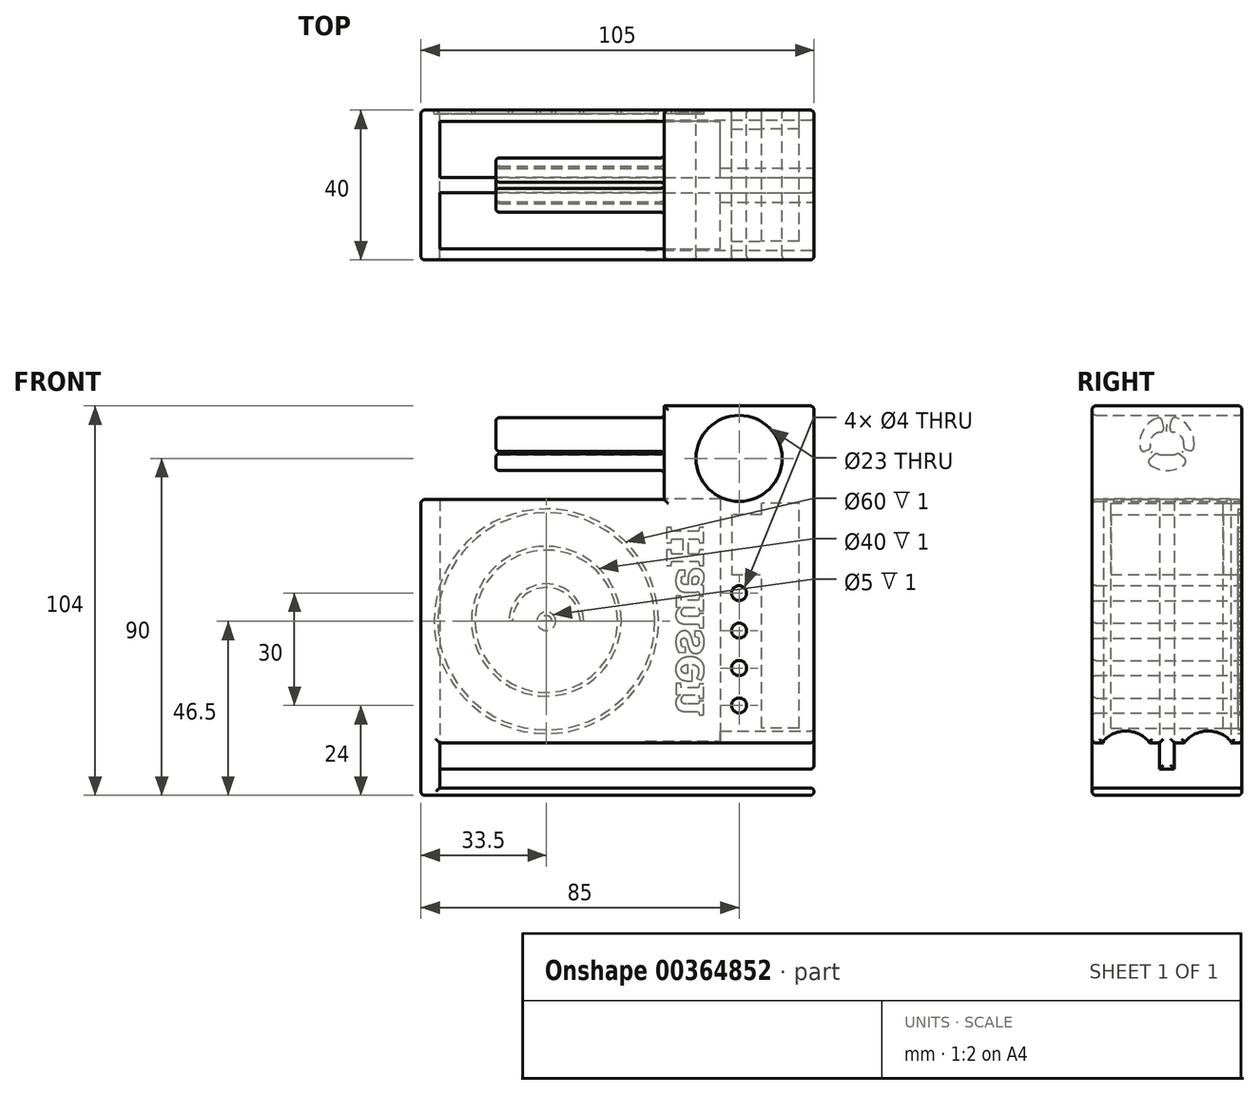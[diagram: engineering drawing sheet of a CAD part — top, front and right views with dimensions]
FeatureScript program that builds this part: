
annotation { "Feature Type Name" : "Feature", "Feature Type Description" : "" }
export const myFeature = defineFeature(function(context is Context, id is Id, definition is map)
    precondition{}
    {
        {
            var Q0;
            Q0=qCreatedBy(makeId("Front.planeOp"),FACE);
            var sketch = newSketch(context, id + "F0", { "sketchPlane" : qUnion([Q0])});
            skLineSegment(sketch, "E0.bottom", {"start": v(20, -45) * mm, "end": v(-20, -45) * mm});
            skLineSegment(sketch, "E0.top", {"start": v(20, 45) * mm, "end": v(-20, 45) * mm});
            skLineSegment(sketch, "E0.left", {"start": v(20, -45) * mm, "end": v(20, 45) * mm});
            skLineSegment(sketch, "E0.right", {"start": v(-20, -45) * mm, "end": v(-20, 45) * mm});
            skPoint(sketch, "E0.middle", {"position": v(0, 0) * mm});
            skLineSegment(sketch, "E1", {"start": v(0, 45) * mm, "end": v(0, 31) * mm});
            skCircle(sketch, "E2", {"center": v(0, 31) * mm, "radius": 11.5 * mm});
            skLineSegment(sketch, "E3", {"start": v(0, -45) * mm, "end": v(0, -35) * mm});
            skLineSegment(sketch, "E4", {"start": v(0, -35) * mm, "end": v(0, -25) * mm});
            skLineSegment(sketch, "E5", {"start": v(0, -25) * mm, "end": v(0, -15) * mm});
            skLineSegment(sketch, "E6", {"start": v(0, -15) * mm, "end": v(0, -5) * mm});
            skLineSegment(sketch, "E7", {"start": v(0, -5) * mm, "end": v(0, 5) * mm});
            skCircle(sketch, "E8", {"center": v(0, -35) * mm, "radius": 2 * mm});
            skCircle(sketch, "E9", {"center": v(0, -25) * mm, "radius": 2 * mm});
            skCircle(sketch, "E10", {"center": v(0, -15) * mm, "radius": 2 * mm});
            skCircle(sketch, "E11", {"center": v(0, -5) * mm, "radius": 2 * mm});
            skSolve(sketch);
        }
        {
            var Q0;
            {var subQ9=sQuery(id+"F0.wireOp",EDGE,"E0.left");Q0=makeQuery(id+"F0.imprint","IMPRINT",FACE,{"disambiguationData":[TD([[makeQuery(id+"F0.imprint","IMPRINT",EDGE,{"derivedFrom":subQ9}),1.0]])]});}
            extrude(context, id + "F1", {"entities" : qUnion([Q0]), "depth" : 40 * mm});
        }
        {
            var Q0;
            Q0=makeQuery(id+"F1.opExtrude","SWEPT_FACE",FACE,{"disambiguationData":[OSD([sQuery(id+"F0.wireOp",EDGE,"E0.right")])]});
            var sketch = newSketch(context, id + "F2", { "sketchPlane" : qUnion([Q0])});
            skLineSegment(sketch, "E12", {"start": v(20, 35) * mm, "end": v(7.42, 30.91) * mm});
            skLineSegment(sketch, "E13", {"start": v(20, 35) * mm, "end": v(21.83, 43.62) * mm});
            skLineSegment(sketch, "E14", {"start": v(20, 35) * mm, "end": v(30.16, 25.85) * mm});
            skCircle(sketch, "E15", {"center": v(20, 35) * mm, "radius": 7.25 * mm});
            skLineSegment(sketch, "E16", {"start": v(20, 35) * mm, "end": v(20, 38) * mm});
            skLineSegment(sketch, "E17", {"start": v(20, 38) * mm, "end": v(18.5, 38) * mm});
            skLineSegment(sketch, "E18", {"start": v(18.5, 38) * mm, "end": v(21.5, 38) * mm});
            skPoint(sketch, "E18.endSnap0", {"position": v(19.25, 38) * mm});
            skLineSegment(sketch, "E19", {"start": v(21.5, 38) * mm, "end": v(21.5, 32) * mm});
            skLineSegment(sketch, "E20", {"start": v(21.5, 32) * mm, "end": v(18.5, 32) * mm});
            skLineSegment(sketch, "E21", {"start": v(18.5, 32) * mm, "end": v(18.5, 38) * mm});
            skArc(sketch, "E22", {"start": v(18.5, 38) * mm, "mid": v(15.5, 35) * mm, "end": v(18.5, 32) * mm});
            skArc(sketch, "E23", {"start": v(21.5, 32) * mm, "mid": v(24.5, 35) * mm, "end": v(21.5, 38) * mm});
            skLineSegment(sketch, "E24", {"start": v(8.8, 25.44) * mm, "end": v(20, 35) * mm});
            skLineSegment(sketch, "E25", {"start": v(20, 35) * mm, "end": v(31.2, 31.03) * mm});
            skLineSegment(sketch, "E26", {"start": v(20, 35) * mm, "end": v(23.11, 43.8) * mm, "construction": true});
            skLineSegment(sketch, "E27", {"start": v(20, 35) * mm, "end": v(18.34, 43.94) * mm});
            skLineSegment(sketch, "E28", {"start": v(0, 45) * mm, "end": v(40, 45) * mm});
            skLineSegment(sketch, "E29", {"start": v(40, 45) * mm, "end": v(20, 45) * mm});
            skLineSegment(sketch, "E30", {"start": v(20, 45) * mm, "end": v(20, 35) * mm});
            skSolve(sketch);
        }
        {
            var Q0;
            {var subQ5=sQuery(id+"F2.wireOp",EDGE,"E12");var subQ7=sQuery(id+"F2.wireOp",EDGE,"E15");var subQ8=makeQuery(id+"F2.imprint","INTERSECT",VERTEX,{"derivedFrom":[subQ5,subQ7]});Q0=makeQuery(id+"F2.imprint","IMPRINT",FACE,{"disambiguationData":[TD([[makeQuery(id+"F2.imprint","IMPRINT",EDGE,{"disambiguationData":[TD([[subQ8,1.0]])],"derivedFrom":subQ5}),-1.0]])]});}
            var Q1;
            {var subQ1=sQuery(id+"F2.wireOp",EDGE,"E20");Q1=makeQuery(id+"F2.imprint","IMPRINT",FACE,{"disambiguationData":[TD([[makeQuery(id+"F2.imprint","IMPRINT",EDGE,{"derivedFrom":subQ1}),1.0]])]});}
            var Q2;
            {var subQ1=sQuery(id+"F2.wireOp",EDGE,"E18");var subQ5=sQuery(id+"F2.wireOp",EDGE,"E13");var subQ6=makeQuery(id+"F2.imprint","INTERSECT",VERTEX,{"derivedFrom":[subQ5,subQ1]});Q2=makeQuery(id+"F2.imprint","IMPRINT",FACE,{"disambiguationData":[TD([[makeQuery(id+"F2.imprint","IMPRINT",EDGE,{"disambiguationData":[TD([[subQ6,-1.0]])],"derivedFrom":subQ5}),-1.0]])]});}
            extrude(context, id + "F3", {"entities" : qUnion([Q0, Q1, Q2]), "operationType" : NewBodyOperationType.ADD, "depth" : 45 * mm});
        }
        {
            var Q0;
            Q0=makeQuery(id+"F3.opExtrude","SWEPT_EDGE",EDGE,{"disambiguationData":[OSD([sQuery(id+"F2.wireOp",EDGE,"E15"),sQuery(id+"F2.wireOp",EDGE,"E27")])]});
            var Q1;
            Q1=makeQuery(id+"F3.opExtrude","SWEPT_EDGE",EDGE,{"disambiguationData":[OSD([sQuery(id+"F2.wireOp",EDGE,"E13"),sQuery(id+"F2.wireOp",EDGE,"E15")])]});
            var Q2;
            Q2=makeQuery(id+"F3.opExtrude","SWEPT_EDGE",EDGE,{"disambiguationData":[OSD([sQuery(id+"F2.wireOp",EDGE,"E13"),sQuery(id+"F2.wireOp",EDGE,"E18")])]});
            var Q3;
            Q3=makeQuery(id+"F3.opExtrude","SWEPT_EDGE",EDGE,{"disambiguationData":[OSD([sQuery(id+"F2.wireOp",EDGE,"E12"),sQuery(id+"F2.wireOp",EDGE,"E15")])]});
            var Q4;
            Q4=makeQuery(id+"F3.opExtrude","SWEPT_EDGE",EDGE,{"disambiguationData":[OSD([sQuery(id+"F2.wireOp",EDGE,"E18"),sQuery(id+"F2.wireOp",EDGE,"E27")])]});
            var Q5;
            Q5=makeQuery(id+"F3.opExtrude","SWEPT_EDGE",EDGE,{"disambiguationData":[OSD([sQuery(id+"F2.wireOp",EDGE,"E12"),sQuery(id+"F2.wireOp",EDGE,"E22")])]});
            var Q6;
            Q6=makeQuery(id+"F3.opExtrude","SWEPT_EDGE",EDGE,{"disambiguationData":[OSD([sQuery(id+"F2.wireOp",EDGE,"E22"),sQuery(id+"F2.wireOp",EDGE,"E24")])]});
            var Q7;
            Q7=makeQuery(id+"F3.opExtrude","SWEPT_EDGE",EDGE,{"disambiguationData":[OSD([sQuery(id+"F2.wireOp",EDGE,"E15"),sQuery(id+"F2.wireOp",EDGE,"E24")])]});
            var Q8;
            Q8=makeQuery(id+"F3.opExtrude","SWEPT_EDGE",EDGE,{"disambiguationData":[OSD([sQuery(id+"F2.wireOp",EDGE,"E14"),sQuery(id+"F2.wireOp",EDGE,"E23")])]});
            var Q9;
            Q9=makeQuery(id+"F3.opExtrude","SWEPT_EDGE",EDGE,{"disambiguationData":[OSD([sQuery(id+"F2.wireOp",EDGE,"E14"),sQuery(id+"F2.wireOp",EDGE,"E15")])]});
            var Q10;
            Q10=makeQuery(id+"F3.opExtrude","SWEPT_EDGE",EDGE,{"disambiguationData":[OSD([sQuery(id+"F2.wireOp",EDGE,"E23"),sQuery(id+"F2.wireOp",EDGE,"E25")])]});
            var Q11;
            Q11=makeQuery(id+"F3.opExtrude","SWEPT_EDGE",EDGE,{"disambiguationData":[OSD([sQuery(id+"F2.wireOp",EDGE,"E15"),sQuery(id+"F2.wireOp",EDGE,"E25")])]});
            fillet(context, id + "F4", {"entities" : qUnion([Q0, Q1, Q2, Q3, Q4, Q5, Q6, Q7, Q8, Q9, Q10, Q11]), "radius" : 1 * mm, "tangentPropagation" : true, "allowEdgeOverflow" : false});
        }
        {
            var Q0;
            Q0=makeQuery(id+"F3.opExtrude","CAP_FACE",FACE,{"disambiguationData":[OSD([sQuery(id+"F2.wireOp",EDGE,"E12"),sQuery(id+"F2.wireOp",EDGE,"E15"),sQuery(id+"F2.wireOp",EDGE,"E18"),sQuery(id+"F2.wireOp",EDGE,"E22"),sQuery(id+"F2.wireOp",EDGE,"E27")])],"isStart":false});
            var Q1;
            {var subQ0=sQuery(id+"F2.wireOp",EDGE,"E15");Q1=makeQuery(id+"F3.opExtrude","SWEPT_FACE",FACE,{"disambiguationData":[OSD([subQ0]),TDD([makeQuery(id+"F2.imprint","IMPRINT",EDGE,{"disambiguationData":[TD([[makeQuery(id+"F2.imprint","INTERSECT",VERTEX,{"derivedFrom":[sQuery(id+"F2.wireOp",EDGE,"E12"),subQ0]}),1.0]])],"derivedFrom":subQ0})])]});}
            var Q2;
            {var subQ0=sQuery(id+"F2.wireOp",EDGE,"E15");Q2=makeQuery(id+"F3.opExtrude","SWEPT_FACE",FACE,{"disambiguationData":[OSD([subQ0]),TDD([makeQuery(id+"F2.imprint","IMPRINT",EDGE,{"disambiguationData":[TD([[makeQuery(id+"F2.imprint","INTERSECT",VERTEX,{"derivedFrom":[subQ0,sQuery(id+"F2.wireOp",EDGE,"E25")]}),-1.0]])],"derivedFrom":subQ0})])]});}
            var Q3;
            {var subQ0=sQuery(id+"F2.wireOp",EDGE,"E15");Q3=makeQuery(id+"F3.opExtrude","SWEPT_FACE",FACE,{"disambiguationData":[OSD([subQ0]),TDD([makeQuery(id+"F2.imprint","IMPRINT",EDGE,{"disambiguationData":[TD([[makeQuery(id+"F2.imprint","INTERSECT",VERTEX,{"derivedFrom":[sQuery(id+"F2.wireOp",EDGE,"E14"),subQ0]}),1.0]])],"derivedFrom":subQ0})])]});}
            fillet(context, id + "F5", {"entities" : qUnion([Q0, Q1, Q2, Q3]), "radius" : 1 * mm, "tangentPropagation" : true, "allowEdgeOverflow" : false});
        }
        {
            var Q0;
            Q0=makeQuery(id+"F5.opFillet","SPLIT",FACE,{"disambiguationData":[OD(0.0)],"derivedFrom":makeQuery(id+"F1.opExtrude","SWEPT_FACE",FACE,{"disambiguationData":[OSD([sQuery(id+"F0.wireOp",EDGE,"E0.right")])]})});
            var sketch = newSketch(context, id + "F6", { "sketchPlane" : qUnion([Q0])});
            skLineSegment(sketch, "E31.bottom", {"start": v(0, -45) * mm, "end": v(40, -45) * mm});
            skLineSegment(sketch, "E31.top", {"start": v(0, 20) * mm, "end": v(40, 20) * mm});
            skLineSegment(sketch, "E31.left", {"start": v(0, -45) * mm, "end": v(0, 20) * mm});
            skLineSegment(sketch, "E31.right", {"start": v(40, -45) * mm, "end": v(40, 20) * mm});
            skSolve(sketch);
        }
        {
            var Q0;
            Q0 = qSketchRegion(id + "F6", true);
            extrude(context, id + "F7", {"entities" : qUnion([Q0]), "operationType" : NewBodyOperationType.ADD, "depth" : 65 * mm});
        }
        {
            var Q0;
            Q0=makeQuery(id+"F7.boolean.opBoolean","MERGE",FACE,{"derivedFrom":[makeQuery(id+"F1.opExtrude","SWEPT_FACE",FACE,{"disambiguationData":[OSD([sQuery(id+"F0.wireOp",EDGE,"E0.bottom")])]}),makeQuery(id+"F7.opExtrude","SWEPT_FACE",FACE,{"disambiguationData":[OSD([sQuery(id+"F6.wireOp",EDGE,"E31.bottom")])]})]});
            var sketch = newSketch(context, id + "F8", { "sketchPlane" : qUnion([Q0])});
            skLineSegment(sketch, "E32", {"start": v(-85, 0) * mm, "end": v(-80, 0) * mm});
            skLineSegment(sketch, "E33", {"start": v(-80, 0) * mm, "end": v(-80, 40) * mm});
            skLineSegment(sketch, "E34", {"start": v(-80, 40) * mm, "end": v(-80, 37) * mm});
            skLineSegment(sketch, "E35", {"start": v(-80, 37) * mm, "end": v(-5, 37) * mm});
            skLineSegment(sketch, "E36", {"start": v(-5, 37) * mm, "end": v(-5, 3) * mm});
            skLineSegment(sketch, "E37", {"start": v(-5, 3) * mm, "end": v(-80, 3) * mm});
            skLineSegment(sketch, "E38", {"start": v(-80, 3) * mm, "end": v(-80, 18) * mm});
            skLineSegment(sketch, "E39", {"start": v(-80, 18) * mm, "end": v(-5, 18) * mm});
            skLineSegment(sketch, "E40", {"start": v(-80, 37) * mm, "end": v(-80, 22) * mm});
            skLineSegment(sketch, "E41", {"start": v(-80, 22) * mm, "end": v(-5, 22) * mm});
            skSolve(sketch);
        }
        {
            var Q0;
            {var subQ0=sQuery(id+"F8.wireOp",EDGE,"E35");Q0=makeQuery(id+"F8.imprint","IMPRINT",FACE,{"disambiguationData":[TD([[makeQuery(id+"F8.imprint","IMPRINT",EDGE,{"derivedFrom":subQ0}),-1.0]])]});}
            var Q1;
            {var subQ0=sQuery(id+"F8.wireOp",EDGE,"E37");Q1=makeQuery(id+"F8.imprint","IMPRINT",FACE,{"disambiguationData":[TD([[makeQuery(id+"F8.imprint","IMPRINT",EDGE,{"derivedFrom":subQ0}),-1.0]])]});}
            extrude(context, id + "F9", {"entities" : qUnion([Q0, Q1]), "operationType" : NewBodyOperationType.REMOVE, "oppositeDirection" : true, "depth" : 65.1 * mm});
        }
        {
            var Q0;
            Q0=makeQuery(id+"F7.boolean.opBoolean","MERGE",FACE,{"derivedFrom":[makeQuery(id+"F1.opExtrude","SWEPT_FACE",FACE,{"disambiguationData":[OSD([sQuery(id+"F0.wireOp",EDGE,"E0.bottom")])]}),makeQuery(id+"F7.opExtrude","SWEPT_FACE",FACE,{"disambiguationData":[OSD([sQuery(id+"F6.wireOp",EDGE,"E31.bottom")])]})]});
            var sketch = newSketch(context, id + "F10", { "sketchPlane" : qUnion([Q0])});
            skLineSegment(sketch, "E42.bottom", {"start": v(-85, 40) * mm, "end": v(-80, 40) * mm});
            skLineSegment(sketch, "E42.top", {"start": v(-85, 0) * mm, "end": v(-80, 0) * mm});
            skLineSegment(sketch, "E42.left", {"start": v(-85, 40) * mm, "end": v(-85, 0) * mm});
            skLineSegment(sketch, "E42.right", {"start": v(-80, 40) * mm, "end": v(-80, 0) * mm});
            skSolve(sketch);
        }
        {
            var Q0;
            Q0 = qSketchRegion(id + "F10", true);
            extrude(context, id + "F11", {"entities" : qUnion([Q0]), "operationType" : NewBodyOperationType.ADD, "depth" : 12 * mm});
        }
        {
            var Q0;
            Q0=makeQuery(id+"F7.boolean.opBoolean","MERGE",FACE,{"derivedFrom":[makeQuery(id+"F1.opExtrude","SWEPT_FACE",FACE,{"disambiguationData":[OSD([sQuery(id+"F0.wireOp",EDGE,"E0.bottom")])]}),makeQuery(id+"F7.opExtrude","SWEPT_FACE",FACE,{"disambiguationData":[OSD([sQuery(id+"F6.wireOp",EDGE,"E31.bottom")])]})]});
            var sketch = newSketch(context, id + "F12", { "sketchPlane" : qUnion([Q0])});
            skLineSegment(sketch, "E43.bottom", {"start": v(-80, 22) * mm, "end": v(20, 22) * mm});
            skLineSegment(sketch, "E43.top", {"start": v(-80, 18) * mm, "end": v(20, 18) * mm});
            skLineSegment(sketch, "E43.left", {"start": v(-80, 22) * mm, "end": v(-80, 18) * mm});
            skLineSegment(sketch, "E43.right", {"start": v(20, 22) * mm, "end": v(20, 18) * mm});
            skSolve(sketch);
        }
        {
            var Q0;
            {var subQ5=sQuery(id+"F12.wireOp",EDGE,"E43.left");Q0=makeQuery(id+"F12.imprint","IMPRINT",FACE,{"disambiguationData":[TD([[makeQuery(id+"F12.imprint","IMPRINT",EDGE,{"derivedFrom":subQ5}),1.0]])]});}
            extrude(context, id + "F13", {"entities" : qUnion([Q0]), "operationType" : NewBodyOperationType.ADD, "depth" : 7 * mm});
        }
        {
            var Q0;
            Q0=makeQuery(id+"F11.opExtrude","CAP_FACE",FACE,{"disambiguationData":[OSD([sQuery(id+"F10.wireOp",EDGE,"E42.bottom"),sQuery(id+"F10.wireOp",EDGE,"E42.top"),sQuery(id+"F10.wireOp",EDGE,"E42.left"),sQuery(id+"F10.wireOp",EDGE,"E42.right")])],"isStart":false});
            var sketch = newSketch(context, id + "F14", { "sketchPlane" : qUnion([Q0])});
            skLineSegment(sketch, "E44.bottom", {"start": v(-85, 0) * mm, "end": v(20, 0) * mm});
            skLineSegment(sketch, "E44.top", {"start": v(-85, 40) * mm, "end": v(20, 40) * mm});
            skLineSegment(sketch, "E44.left", {"start": v(-85, 0) * mm, "end": v(-85, 40) * mm});
            skLineSegment(sketch, "E44.right", {"start": v(20, 0) * mm, "end": v(20, 40) * mm});
            skSolve(sketch);
        }
        {
            var Q0;
            Q0 = qSketchRegion(id + "F14", true);
            extrude(context, id + "F15", {"entities" : qUnion([Q0]), "operationType" : NewBodyOperationType.ADD, "depth" : 2 * mm});
        }
        {
            var Q0;
            Q0=makeQuery(id+"F13.boolean.opBoolean","MERGE",FACE,{"derivedFrom":[makeQuery(id+"F1.opExtrude","SWEPT_FACE",FACE,{"disambiguationData":[OSD([sQuery(id+"F0.wireOp",EDGE,"E0.left")])]}),makeQuery(id+"F13.opExtrude","SWEPT_FACE",FACE,{"disambiguationData":[OSD([sQuery(id+"F12.wireOp",EDGE,"E43.right")])]})]});
            var sketch = newSketch(context, id + "F16", { "sketchPlane" : qUnion([Q0])});
            skLineSegment(sketch, "E45", {"start": v(-40, -45) * mm, "end": v(-40, -59) * mm});
            skLineSegment(sketch, "E46", {"start": v(-40, -59) * mm, "end": v(-31, -59) * mm});
            skLineSegment(sketch, "E47", {"start": v(-31, -59) * mm, "end": v(-31, -57) * mm});
            skLineSegment(sketch, "E48", {"start": v(-31, -57) * mm, "end": v(-31, -49.8) * mm});
            skCircle(sketch, "E49", {"center": v(-31, -49.8) * mm, "radius": 8 * mm});
            skLineSegment(sketch, "E50", {"start": v(-31, -49.8) * mm, "end": v(-9, -49.8) * mm});
            skLineSegment(sketch, "E51", {"start": v(-9, -49.8) * mm, "end": v(-9, -45) * mm});
            skLineSegment(sketch, "E52", {"start": v(-9, -45) * mm, "end": v(0, -45) * mm});
            skCircle(sketch, "E53", {"center": v(-9, -49.8) * mm, "radius": 8 * mm});
            skSolve(sketch);
        }
        {
            var Q0;
            {var subQ0=sQuery(id+"F16.wireOp",EDGE,"E49");var subQ1=sQuery(id+"F0.wireOp",EDGE,"E0.left");var subQ2=sQuery(id+"F0.wireOp",EDGE,"E0.bottom");var subQ3=makeQuery(id+"F13.boolean.opBoolean","SPLIT",EDGE,{"disambiguationData":[TD([makeQuery(id+"F7.opExtrude","SWEPT_FACE",FACE,{"disambiguationData":[OSD([sQuery(id+"F6.wireOp",EDGE,"E31.right")])]})])],"derivedFrom":makeQuery(id+"F1.opExtrude","SWEPT_EDGE",EDGE,{"disambiguationData":[OSD([subQ2,subQ1])]})});var subQ4=makeQuery(id+"F16.imprint","INTERSECT",VERTEX,{"disambiguationData":[OD(0.0)],"derivedFrom":[subQ3,subQ0]});Q0=makeQuery(id+"F16.imprint","IMPRINT",FACE,{"disambiguationData":[TD([[makeQuery(id+"F16.imprint","IMPRINT",EDGE,{"disambiguationData":[TD([[subQ4,-1.0]])],"derivedFrom":subQ0}),1.0]])]});}
            var Q1;
            {var subQ0=sQuery(id+"F16.wireOp",EDGE,"E52");var subQ5=sQuery(id+"F16.wireOp",EDGE,"E53");var subQ6=makeQuery(id+"F16.imprint","INTERSECT",VERTEX,{"derivedFrom":[subQ0,subQ5]});Q1=makeQuery(id+"F16.imprint","IMPRINT",FACE,{"disambiguationData":[TD([[makeQuery(id+"F16.imprint","IMPRINT",EDGE,{"disambiguationData":[TD([[subQ6,-1.0]])],"derivedFrom":subQ5}),1.0]])]});}
            extrude(context, id + "F17", {"entities" : qUnion([Q0, Q1]), "operationType" : NewBodyOperationType.REMOVE, "oppositeDirection" : true, "depth" : 45 * mm});
        }
        {
            var Q0;
            Q0=makeQuery(id+"F15.boolean.opBoolean","MERGE",EDGE,{"derivedFrom":[makeQuery(id+"F11.boolean.opBoolean","MERGE",EDGE,{"derivedFrom":[makeQuery(id+"F7.opExtrude","CAP_EDGE",EDGE,{"disambiguationData":[OSD([sQuery(id+"F6.wireOp",EDGE,"E31.right")])],"isStart":false}),makeQuery(id+"F11.opExtrude","SWEPT_EDGE",EDGE,{"disambiguationData":[OSD([sQuery(id+"F10.wireOp",EDGE,"E42.bottom"),sQuery(id+"F10.wireOp",EDGE,"E42.left")])]})]}),makeQuery(id+"F15.opExtrude","SWEPT_EDGE",EDGE,{"disambiguationData":[OSD([sQuery(id+"F14.wireOp",EDGE,"E44.top"),sQuery(id+"F14.wireOp",EDGE,"E44.left")])]})]});
            var Q1;
            Q1=makeQuery(id+"F15.opExtrude","CAP_EDGE",EDGE,{"disambiguationData":[OSD([sQuery(id+"F14.wireOp",EDGE,"E44.top")])],"isStart":false});
            var Q2;
            Q2=makeQuery(id+"F11.opExtrude","SWEPT_EDGE",EDGE,{"disambiguationData":[OSD([sQuery(id+"F0.wireOp",EDGE,"E0.bottom"),sQuery(id+"F6.wireOp",EDGE,"E31.bottom"),sQuery(id+"F6.wireOp",EDGE,"E31.right"),sQuery(id+"F10.wireOp",EDGE,"E42.bottom"),sQuery(id+"F10.wireOp",EDGE,"E42.right")])]});
            var Q3;
            Q3=makeQuery(id+"F15.boolean.opBoolean","MERGE",FACE,{"derivedFrom":[makeQuery(id+"F11.boolean.opBoolean","MERGE",FACE,{"derivedFrom":[makeQuery(id+"F7.boolean.opBoolean","MERGE",FACE,{"derivedFrom":[makeQuery(id+"F1.opExtrude","CAP_FACE",FACE,{"disambiguationData":[OSD([sQuery(id+"F0.wireOp",EDGE,"E0.bottom"),sQuery(id+"F0.wireOp",EDGE,"E0.top"),sQuery(id+"F0.wireOp",EDGE,"E0.left"),sQuery(id+"F0.wireOp",EDGE,"E0.right"),sQuery(id+"F0.wireOp",EDGE,"E2"),sQuery(id+"F0.wireOp",EDGE,"E8"),sQuery(id+"F0.wireOp",EDGE,"E9"),sQuery(id+"F0.wireOp",EDGE,"E10"),sQuery(id+"F0.wireOp",EDGE,"E11")])],"isStart":false}),makeQuery(id+"F7.opExtrude","SWEPT_FACE",FACE,{"disambiguationData":[OSD([sQuery(id+"F6.wireOp",EDGE,"E31.right")])]})]}),makeQuery(id+"F11.opExtrude","SWEPT_FACE",FACE,{"disambiguationData":[OSD([sQuery(id+"F10.wireOp",EDGE,"E42.bottom")])]})]}),makeQuery(id+"F15.opExtrude","SWEPT_FACE",FACE,{"disambiguationData":[OSD([sQuery(id+"F14.wireOp",EDGE,"E44.top")])]})]});
            var Q4;
            Q4=makeQuery(id+"F15.boolean.opBoolean","MERGE",FACE,{"derivedFrom":[makeQuery(id+"F11.boolean.opBoolean","MERGE",FACE,{"derivedFrom":[makeQuery(id+"F7.boolean.opBoolean","MERGE",FACE,{"derivedFrom":[makeQuery(id+"F1.opExtrude","CAP_FACE",FACE,{"disambiguationData":[OSD([sQuery(id+"F0.wireOp",EDGE,"E0.bottom"),sQuery(id+"F0.wireOp",EDGE,"E0.top"),sQuery(id+"F0.wireOp",EDGE,"E0.left"),sQuery(id+"F0.wireOp",EDGE,"E0.right"),sQuery(id+"F0.wireOp",EDGE,"E2"),sQuery(id+"F0.wireOp",EDGE,"E8"),sQuery(id+"F0.wireOp",EDGE,"E9"),sQuery(id+"F0.wireOp",EDGE,"E10"),sQuery(id+"F0.wireOp",EDGE,"E11")])],"isStart":true}),makeQuery(id+"F7.opExtrude","SWEPT_FACE",FACE,{"disambiguationData":[OSD([sQuery(id+"F6.wireOp",EDGE,"E31.left")])]})]}),makeQuery(id+"F11.opExtrude","SWEPT_FACE",FACE,{"disambiguationData":[OSD([sQuery(id+"F10.wireOp",EDGE,"E42.top")])]})]}),makeQuery(id+"F15.opExtrude","SWEPT_FACE",FACE,{"disambiguationData":[OSD([sQuery(id+"F14.wireOp",EDGE,"E44.bottom")])]})]});
            var Q5;
            Q5=makeQuery(id+"F15.boolean.opBoolean","MERGE",FACE,{"derivedFrom":[makeQuery(id+"F11.boolean.opBoolean","MERGE",FACE,{"derivedFrom":[makeQuery(id+"F7.opExtrude","CAP_FACE",FACE,{"disambiguationData":[OSD([sQuery(id+"F6.wireOp",EDGE,"E31.bottom"),sQuery(id+"F6.wireOp",EDGE,"E31.top"),sQuery(id+"F6.wireOp",EDGE,"E31.left"),sQuery(id+"F6.wireOp",EDGE,"E31.right")])],"isStart":false}),makeQuery(id+"F11.opExtrude","SWEPT_FACE",FACE,{"disambiguationData":[OSD([sQuery(id+"F10.wireOp",EDGE,"E42.left")])]})]}),makeQuery(id+"F15.opExtrude","SWEPT_FACE",FACE,{"disambiguationData":[OSD([sQuery(id+"F14.wireOp",EDGE,"E44.left")])]})]});
            var Q6;
            Q6=makeQuery(id+"F13.boolean.opBoolean","MERGE",FACE,{"derivedFrom":[makeQuery(id+"F1.opExtrude","SWEPT_FACE",FACE,{"disambiguationData":[OSD([sQuery(id+"F0.wireOp",EDGE,"E0.left")])]}),makeQuery(id+"F13.opExtrude","SWEPT_FACE",FACE,{"disambiguationData":[OSD([sQuery(id+"F12.wireOp",EDGE,"E43.right")])]})]});
            var Q7;
            Q7=makeQuery(id+"F15.opExtrude","SWEPT_FACE",FACE,{"disambiguationData":[OSD([sQuery(id+"F14.wireOp",EDGE,"E44.right")])]});
            fillet(context, id + "F18", {"entities" : qUnion([Q0, Q1, Q2, Q3, Q4, Q5, Q6, Q7]), "radius" : 1 * mm, "tangentPropagation" : true, "allowEdgeOverflow" : false});
        }
        {
            var Q0;
            Q0=makeQuery(id+"F15.boolean.opBoolean","MERGE",FACE,{"derivedFrom":[makeQuery(id+"F11.boolean.opBoolean","MERGE",FACE,{"derivedFrom":[makeQuery(id+"F7.boolean.opBoolean","MERGE",FACE,{"derivedFrom":[makeQuery(id+"F1.opExtrude","CAP_FACE",FACE,{"disambiguationData":[OSD([sQuery(id+"F0.wireOp",EDGE,"E0.bottom"),sQuery(id+"F0.wireOp",EDGE,"E0.top"),sQuery(id+"F0.wireOp",EDGE,"E0.left"),sQuery(id+"F0.wireOp",EDGE,"E0.right"),sQuery(id+"F0.wireOp",EDGE,"E2"),sQuery(id+"F0.wireOp",EDGE,"E8"),sQuery(id+"F0.wireOp",EDGE,"E9"),sQuery(id+"F0.wireOp",EDGE,"E10"),sQuery(id+"F0.wireOp",EDGE,"E11")])],"isStart":true}),makeQuery(id+"F7.opExtrude","SWEPT_FACE",FACE,{"disambiguationData":[OSD([sQuery(id+"F6.wireOp",EDGE,"E31.left")])]})]}),makeQuery(id+"F11.opExtrude","SWEPT_FACE",FACE,{"disambiguationData":[OSD([sQuery(id+"F10.wireOp",EDGE,"E42.top")])]})]}),makeQuery(id+"F15.opExtrude","SWEPT_FACE",FACE,{"disambiguationData":[OSD([sQuery(id+"F14.wireOp",EDGE,"E44.bottom")])]})]});
            var sketch = newSketch(context, id + "F19", { "sketchPlane" : qUnion([Q0])});
            skLineSegment(sketch, "E54", {"start": v(19, 19) * mm, "end": v(19, -44) * mm});
            skLineSegment(sketch, "E55", {"start": v(84, 19) * mm, "end": v(19, 19) * mm});
            skLineSegment(sketch, "E56", {"start": v(19, -44) * mm, "end": v(84, -44) * mm});
            skCircle(sketch, "E57", {"center": v(51.5, -12.5) * mm, "radius": 30 * mm});
            skCircle(sketch, "E58", {"center": v(51.5, -12.5) * mm, "radius": 20 * mm});
            skCircle(sketch, "E59", {"center": v(51.5, -12.5) * mm, "radius": 10 * mm});
            skCircle(sketch, "E60", {"center": v(51.5, -12.5) * mm, "radius": 2.5 * mm});
            skLineSegment(sketch, "E61", {"start": v(51.5, 19) * mm, "end": v(51.5, -44) * mm});
            skLineSegment(sketch, "E62", {"start": v(19, -12.5) * mm, "end": v(84, -12.5) * mm});
            skCircle(sketch, "E63", {"center": v(51.5, -12.5) * mm, "radius": 29 * mm});
            skCircle(sketch, "E64", {"center": v(51.5, -12.5) * mm, "radius": 19 * mm});
            skCircle(sketch, "E65", {"center": v(51.5, -12.5) * mm, "radius": 9 * mm});
            skCircle(sketch, "E66", {"center": v(51.5, -12.5) * mm, "radius": 1.5 * mm});
            skSolve(sketch);
        }
        {
            var Q0;
            {var subQ0=sQuery(id+"F19.wireOp",EDGE,"E61");var subQ1=sQuery(id+"F19.wireOp",EDGE,"E57");var subQ2=makeQuery(id+"F19.imprint","INTERSECT",VERTEX,{"disambiguationData":[OD(0.0)],"derivedFrom":[subQ1,subQ0]});Q0=makeQuery(id+"F19.imprint","IMPRINT",FACE,{"disambiguationData":[TD([[makeQuery(id+"F19.imprint","IMPRINT",EDGE,{"disambiguationData":[TD([[subQ2,-1.0]])],"derivedFrom":subQ1}),1.0]])]});}
            var Q1;
            {var subQ0=sQuery(id+"F19.wireOp",EDGE,"E61");var subQ1=sQuery(id+"F19.wireOp",EDGE,"E58");var subQ2=makeQuery(id+"F19.imprint","INTERSECT",VERTEX,{"disambiguationData":[OD(0.0)],"derivedFrom":[subQ1,subQ0]});Q1=makeQuery(id+"F19.imprint","IMPRINT",FACE,{"disambiguationData":[TD([[makeQuery(id+"F19.imprint","IMPRINT",EDGE,{"disambiguationData":[TD([[subQ2,-1.0]])],"derivedFrom":subQ1}),1.0]])]});}
            var Q2;
            {var subQ0=sQuery(id+"F19.wireOp",EDGE,"E61");var subQ1=sQuery(id+"F19.wireOp",EDGE,"E59");var subQ2=makeQuery(id+"F19.imprint","INTERSECT",VERTEX,{"disambiguationData":[OD(0.0)],"derivedFrom":[subQ1,subQ0]});Q2=makeQuery(id+"F19.imprint","IMPRINT",FACE,{"disambiguationData":[TD([[makeQuery(id+"F19.imprint","IMPRINT",EDGE,{"disambiguationData":[TD([[subQ2,-1.0]])],"derivedFrom":subQ1}),1.0]])]});}
            var Q3;
            {var subQ0=sQuery(id+"F19.wireOp",EDGE,"E62");var subQ1=sQuery(id+"F19.wireOp",EDGE,"E58");var subQ2=makeQuery(id+"F19.imprint","INTERSECT",VERTEX,{"disambiguationData":[OD(1.0)],"derivedFrom":[subQ1,subQ0]});Q3=makeQuery(id+"F19.imprint","IMPRINT",FACE,{"disambiguationData":[TD([[makeQuery(id+"F19.imprint","IMPRINT",EDGE,{"disambiguationData":[TD([[subQ2,-1.0]])],"derivedFrom":subQ1}),1.0]])]});}
            var Q4;
            {var subQ0=sQuery(id+"F19.wireOp",EDGE,"E62");var subQ1=sQuery(id+"F19.wireOp",EDGE,"E57");var subQ2=makeQuery(id+"F19.imprint","INTERSECT",VERTEX,{"disambiguationData":[OD(1.0)],"derivedFrom":[subQ1,subQ0]});Q4=makeQuery(id+"F19.imprint","IMPRINT",FACE,{"disambiguationData":[TD([[makeQuery(id+"F19.imprint","IMPRINT",EDGE,{"disambiguationData":[TD([[subQ2,-1.0]])],"derivedFrom":subQ1}),1.0]])]});}
            var Q5;
            {var subQ0=sQuery(id+"F19.wireOp",EDGE,"E62");var subQ1=sQuery(id+"F19.wireOp",EDGE,"E57");var subQ2=makeQuery(id+"F19.imprint","INTERSECT",VERTEX,{"disambiguationData":[OD(0.0)],"derivedFrom":[subQ1,subQ0]});Q5=makeQuery(id+"F19.imprint","IMPRINT",FACE,{"disambiguationData":[TD([[makeQuery(id+"F19.imprint","IMPRINT",EDGE,{"disambiguationData":[TD([[subQ2,1.0]])],"derivedFrom":subQ1}),1.0]])]});}
            var Q6;
            {var subQ0=sQuery(id+"F19.wireOp",EDGE,"E62");var subQ1=sQuery(id+"F19.wireOp",EDGE,"E58");var subQ2=makeQuery(id+"F19.imprint","INTERSECT",VERTEX,{"disambiguationData":[OD(0.0)],"derivedFrom":[subQ1,subQ0]});Q6=makeQuery(id+"F19.imprint","IMPRINT",FACE,{"disambiguationData":[TD([[makeQuery(id+"F19.imprint","IMPRINT",EDGE,{"disambiguationData":[TD([[subQ2,1.0]])],"derivedFrom":subQ1}),1.0]])]});}
            var Q7;
            {var subQ0=sQuery(id+"F19.wireOp",EDGE,"E62");var subQ1=sQuery(id+"F19.wireOp",EDGE,"E59");var subQ2=makeQuery(id+"F19.imprint","INTERSECT",VERTEX,{"disambiguationData":[OD(1.0)],"derivedFrom":[subQ1,subQ0]});Q7=makeQuery(id+"F19.imprint","IMPRINT",FACE,{"disambiguationData":[TD([[makeQuery(id+"F19.imprint","IMPRINT",EDGE,{"disambiguationData":[TD([[subQ2,-1.0]])],"derivedFrom":subQ1}),1.0]])]});}
            var Q8;
            {var subQ0=sQuery(id+"F19.wireOp",EDGE,"E62");var subQ1=sQuery(id+"F19.wireOp",EDGE,"E59");var subQ2=makeQuery(id+"F19.imprint","INTERSECT",VERTEX,{"disambiguationData":[OD(0.0)],"derivedFrom":[subQ1,subQ0]});Q8=makeQuery(id+"F19.imprint","IMPRINT",FACE,{"disambiguationData":[TD([[makeQuery(id+"F19.imprint","IMPRINT",EDGE,{"disambiguationData":[TD([[subQ2,1.0]])],"derivedFrom":subQ1}),1.0]])]});}
            var Q9;
            {var subQ0=sQuery(id+"F19.wireOp",EDGE,"E61");var subQ1=sQuery(id+"F19.wireOp",EDGE,"E59");var subQ2=makeQuery(id+"F19.imprint","INTERSECT",VERTEX,{"disambiguationData":[OD(0.0)],"derivedFrom":[subQ1,subQ0]});Q9=makeQuery(id+"F19.imprint","IMPRINT",FACE,{"disambiguationData":[TD([[makeQuery(id+"F19.imprint","IMPRINT",EDGE,{"disambiguationData":[TD([[subQ2,1.0]])],"derivedFrom":subQ1}),1.0]])]});}
            var Q10;
            {var subQ0=sQuery(id+"F19.wireOp",EDGE,"E61");var subQ1=sQuery(id+"F19.wireOp",EDGE,"E57");var subQ2=makeQuery(id+"F19.imprint","INTERSECT",VERTEX,{"disambiguationData":[OD(0.0)],"derivedFrom":[subQ1,subQ0]});Q10=makeQuery(id+"F19.imprint","IMPRINT",FACE,{"disambiguationData":[TD([[makeQuery(id+"F19.imprint","IMPRINT",EDGE,{"disambiguationData":[TD([[subQ2,1.0]])],"derivedFrom":subQ1}),1.0]])]});}
            var Q11;
            {var subQ0=sQuery(id+"F19.wireOp",EDGE,"E61");var subQ1=sQuery(id+"F19.wireOp",EDGE,"E58");var subQ2=makeQuery(id+"F19.imprint","INTERSECT",VERTEX,{"disambiguationData":[OD(0.0)],"derivedFrom":[subQ1,subQ0]});Q11=makeQuery(id+"F19.imprint","IMPRINT",FACE,{"disambiguationData":[TD([[makeQuery(id+"F19.imprint","IMPRINT",EDGE,{"disambiguationData":[TD([[subQ2,1.0]])],"derivedFrom":subQ1}),1.0]])]});}
            var Q12;
            {var subQ0=sQuery(id+"F19.wireOp",EDGE,"E62");var subQ1=sQuery(id+"F19.wireOp",EDGE,"E60");var subQ2=makeQuery(id+"F19.imprint","INTERSECT",VERTEX,{"disambiguationData":[OD(1.0)],"derivedFrom":[subQ1,subQ0]});Q12=makeQuery(id+"F19.imprint","IMPRINT",FACE,{"disambiguationData":[TD([[makeQuery(id+"F19.imprint","IMPRINT",EDGE,{"disambiguationData":[TD([[subQ2,-1.0]])],"derivedFrom":subQ1}),1.0]])]});}
            var Q13;
            {var subQ0=sQuery(id+"F19.wireOp",EDGE,"E62");var subQ1=sQuery(id+"F19.wireOp",EDGE,"E60");var subQ2=makeQuery(id+"F19.imprint","INTERSECT",VERTEX,{"disambiguationData":[OD(0.0)],"derivedFrom":[subQ1,subQ0]});Q13=makeQuery(id+"F19.imprint","IMPRINT",FACE,{"disambiguationData":[TD([[makeQuery(id+"F19.imprint","IMPRINT",EDGE,{"disambiguationData":[TD([[subQ2,1.0]])],"derivedFrom":subQ1}),1.0]])]});}
            var Q14;
            {var subQ0=sQuery(id+"F19.wireOp",EDGE,"E61");var subQ1=sQuery(id+"F19.wireOp",EDGE,"E60");var subQ2=makeQuery(id+"F19.imprint","INTERSECT",VERTEX,{"disambiguationData":[OD(0.0)],"derivedFrom":[subQ1,subQ0]});Q14=makeQuery(id+"F19.imprint","IMPRINT",FACE,{"disambiguationData":[TD([[makeQuery(id+"F19.imprint","IMPRINT",EDGE,{"disambiguationData":[TD([[subQ2,1.0]])],"derivedFrom":subQ1}),1.0]])]});}
            var Q15;
            {var subQ0=sQuery(id+"F19.wireOp",EDGE,"E61");var subQ1=sQuery(id+"F19.wireOp",EDGE,"E60");var subQ2=makeQuery(id+"F19.imprint","INTERSECT",VERTEX,{"disambiguationData":[OD(0.0)],"derivedFrom":[subQ1,subQ0]});Q15=makeQuery(id+"F19.imprint","IMPRINT",FACE,{"disambiguationData":[TD([[makeQuery(id+"F19.imprint","IMPRINT",EDGE,{"disambiguationData":[TD([[subQ2,-1.0]])],"derivedFrom":subQ1}),1.0]])]});}
            var Q16;
            {var subQ0=sQuery(id+"F19.wireOp",EDGE,"E66");var subQ1=sQuery(id+"F19.wireOp",EDGE,"E61");var subQ2=makeQuery(id+"F19.imprint","INTERSECT",VERTEX,{"disambiguationData":[OD(0.0)],"derivedFrom":[subQ1,subQ0]});Q16=makeQuery(id+"F19.imprint","IMPRINT",FACE,{"disambiguationData":[TD([[makeQuery(id+"F19.imprint","IMPRINT",EDGE,{"disambiguationData":[TD([[subQ2,-1.0]])],"derivedFrom":subQ1}),-1.0]])]});}
            var Q17;
            {var subQ0=sQuery(id+"F19.wireOp",EDGE,"E66");var subQ1=sQuery(id+"F19.wireOp",EDGE,"E61");var subQ2=makeQuery(id+"F19.imprint","INTERSECT",VERTEX,{"disambiguationData":[OD(0.0)],"derivedFrom":[subQ1,subQ0]});Q17=makeQuery(id+"F19.imprint","IMPRINT",FACE,{"disambiguationData":[TD([[makeQuery(id+"F19.imprint","IMPRINT",EDGE,{"disambiguationData":[TD([[subQ2,-1.0]])],"derivedFrom":subQ1}),1.0]])]});}
            var Q18;
            {var subQ0=sQuery(id+"F19.wireOp",EDGE,"E62");var subQ1=sQuery(id+"F19.wireOp",EDGE,"E61");var subQ2=makeQuery(id+"F19.imprint","INTERSECT",VERTEX,{"derivedFrom":[subQ1,subQ0]});Q18=makeQuery(id+"F19.imprint","IMPRINT",FACE,{"disambiguationData":[TD([[makeQuery(id+"F19.imprint","IMPRINT",EDGE,{"disambiguationData":[TD([[subQ2,-1.0]])],"derivedFrom":subQ1}),1.0]])]});}
            var Q19;
            {var subQ0=sQuery(id+"F19.wireOp",EDGE,"E62");var subQ1=sQuery(id+"F19.wireOp",EDGE,"E61");var subQ2=makeQuery(id+"F19.imprint","INTERSECT",VERTEX,{"derivedFrom":[subQ1,subQ0]});Q19=makeQuery(id+"F19.imprint","IMPRINT",FACE,{"disambiguationData":[TD([[makeQuery(id+"F19.imprint","IMPRINT",EDGE,{"disambiguationData":[TD([[subQ2,-1.0]])],"derivedFrom":subQ1}),-1.0]])]});}
            extrude(context, id + "F20", {"entities" : qUnion([Q0, Q1, Q2, Q3, Q4, Q5, Q6, Q7, Q8, Q9, Q10, Q11, Q12, Q13, Q14, Q15, Q16, Q17, Q18, Q19]), "operationType" : NewBodyOperationType.REMOVE, "oppositeDirection" : true, "depth" : 1 * mm});
        }
        {
            var Q0;
            Q0=makeQuery(id+"F20.boolean.opBoolean","SPLIT",FACE,{"disambiguationData":[TD([makeQuery(id+"F20.opExtrude","SWEPT_FACE",FACE,{"disambiguationData":[OSD([sQuery(id+"F19.wireOp",EDGE,"E58")])]})])],"derivedFrom":makeQuery(id+"F15.boolean.opBoolean","MERGE",FACE,{"derivedFrom":[makeQuery(id+"F11.boolean.opBoolean","MERGE",FACE,{"derivedFrom":[makeQuery(id+"F7.boolean.opBoolean","MERGE",FACE,{"derivedFrom":[makeQuery(id+"F1.opExtrude","CAP_FACE",FACE,{"disambiguationData":[OSD([sQuery(id+"F0.wireOp",EDGE,"E0.bottom"),sQuery(id+"F0.wireOp",EDGE,"E0.top"),sQuery(id+"F0.wireOp",EDGE,"E0.left"),sQuery(id+"F0.wireOp",EDGE,"E0.right"),sQuery(id+"F0.wireOp",EDGE,"E2"),sQuery(id+"F0.wireOp",EDGE,"E8"),sQuery(id+"F0.wireOp",EDGE,"E9"),sQuery(id+"F0.wireOp",EDGE,"E10"),sQuery(id+"F0.wireOp",EDGE,"E11")])],"isStart":true}),makeQuery(id+"F7.opExtrude","SWEPT_FACE",FACE,{"disambiguationData":[OSD([sQuery(id+"F6.wireOp",EDGE,"E31.left")])]})]}),makeQuery(id+"F11.opExtrude","SWEPT_FACE",FACE,{"disambiguationData":[OSD([sQuery(id+"F10.wireOp",EDGE,"E42.top")])]})]}),makeQuery(id+"F15.opExtrude","SWEPT_FACE",FACE,{"disambiguationData":[OSD([sQuery(id+"F14.wireOp",EDGE,"E44.bottom")])]})]})});
            var sketch = newSketch(context, id + "F21", { "sketchPlane" : qUnion([Q0])});
            skText(sketch, "E67", { "text": "Hansen", "fontName": "RobotoSlab-Bold.ttf"});
            const initialGuessF21  = {"E67": [0.00945, 0.0129, 0, -1, 0.01]};
            skSetInitialGuess(sketch, initialGuessF21);
            skSolve(sketch);
        }
        {
            var Q0;
            Q0 = qSketchRegion(id + "F21", true);
            extrude(context, id + "F22", {"entities" : qUnion([Q0]), "operationType" : NewBodyOperationType.REMOVE, "oppositeDirection" : true, "depth" : 1 * mm});
        }
        {
            var Q0;
            {var subQ0=sQuery(id+"F14.wireOp",EDGE,"E44.bottom");var subQ1=makeQuery(id+"F18.opFillet","BLEND_FACE",FACE,{"disambiguationData":[OSD([subQ0])]});var subQ3=sQuery(id+"F10.wireOp",EDGE,"E42.top");var subQ4=sQuery(id+"F6.wireOp",EDGE,"E31.left");var subQ8=sQuery(id+"F0.wireOp",EDGE,"E0.bottom");var subQ11=sQuery(id+"F0.wireOp",EDGE,"E0.right");var subQ13=sQuery(id+"F0.wireOp",EDGE,"E0.left");var subQ15=sQuery(id+"F0.wireOp",EDGE,"E0.top");var subQ19=sQuery(id+"F0.wireOp",EDGE,"E9");var subQ24=sQuery(id+"F0.wireOp",EDGE,"E8");var subQ26=sQuery(id+"F0.wireOp",EDGE,"E2");var subQ28=sQuery(id+"F0.wireOp",EDGE,"E10");var subQ30=sQuery(id+"F0.wireOp",EDGE,"E11");Q0=makeQuery(id+"F22.boolean.opBoolean","SPLIT",FACE,{"disambiguationData":[TD([subQ1])],"derivedFrom":makeQuery(id+"F20.boolean.opBoolean","SPLIT",FACE,{"disambiguationData":[TD([subQ1])],"derivedFrom":makeQuery(id+"F15.boolean.opBoolean","MERGE",FACE,{"derivedFrom":[makeQuery(id+"F11.boolean.opBoolean","MERGE",FACE,{"derivedFrom":[makeQuery(id+"F7.boolean.opBoolean","MERGE",FACE,{"derivedFrom":[makeQuery(id+"F1.opExtrude","CAP_FACE",FACE,{"disambiguationData":[OSD([subQ8,subQ15,subQ13,subQ11,subQ26,subQ24,subQ19,subQ28,subQ30])],"isStart":true}),makeQuery(id+"F7.opExtrude","SWEPT_FACE",FACE,{"disambiguationData":[OSD([subQ4])]})]}),makeQuery(id+"F11.opExtrude","SWEPT_FACE",FACE,{"disambiguationData":[OSD([subQ3])]})]}),makeQuery(id+"F15.opExtrude","SWEPT_FACE",FACE,{"disambiguationData":[OSD([subQ0])]})]})})});}
            var sketch = newSketch(context, id + "F23", { "sketchPlane" : qUnion([Q0])});
            skLineSegment(sketch, "E68", {"start": v(-19, -44) * mm, "end": v(-16, -44) * mm});
            skLineSegment(sketch, "E69", {"start": v(-19, -44) * mm, "end": v(-19, -41) * mm});
            skLineSegment(sketch, "E70", {"start": v(-19, -41) * mm, "end": v(-16, -41) * mm});
            skLineSegment(sketch, "E71", {"start": v(-16, -41) * mm, "end": v(-16, -44) * mm});
            skLineSegment(sketch, "E72.bottom", {"start": v(-16, -41) * mm, "end": v(-6, -41) * mm});
            skLineSegment(sketch, "E72.top", {"start": v(-16, 19) * mm, "end": v(-6, 19) * mm});
            skLineSegment(sketch, "E72.left", {"start": v(-16, -41) * mm, "end": v(-16, 19) * mm});
            skLineSegment(sketch, "E72.right", {"start": v(-6, -41) * mm, "end": v(-6, 19) * mm});
            skLineSegment(sketch, "E73", {"start": v(-6, 19) * mm, "end": v(-6, 16) * mm});
            skLineSegment(sketch, "E74", {"start": v(-6, 16) * mm, "end": v(2, 16) * mm});
            skLineSegment(sketch, "E75", {"start": v(2, 16) * mm, "end": v(2, 0) * mm});
            skLineSegment(sketch, "E76", {"start": v(2, 0) * mm, "end": v(-6, 0) * mm});
            skSolve(sketch);
        }
        {
            var Q0;
            Q0=makeQuery(id+"F23.imprint","IMPRINT",FACE,{"disambiguationData":[TD([[makeQuery(id+"F23.imprint","IMPRINT",EDGE,{"derivedFrom":sQuery(id+"F23.wireOp",EDGE,"E72.bottom")}),1.0]])]});
            var Q1;
            {var subQ0=sQuery(id+"F23.wireOp",EDGE,"E74");Q1=makeQuery(id+"F23.imprint","IMPRINT",FACE,{"disambiguationData":[TD([[makeQuery(id+"F23.imprint","IMPRINT",EDGE,{"derivedFrom":subQ0}),-1.0]])]});}
            extrude(context, id + "F24", {"entities" : qUnion([Q0, Q1]), "operationType" : NewBodyOperationType.REMOVE, "oppositeDirection" : true, "depth" : 35 * mm});
        }
        {
            var Q0;
            {var subQ0=sQuery(id+"F14.wireOp",EDGE,"E44.bottom");var subQ1=makeQuery(id+"F18.opFillet","BLEND_FACE",FACE,{"disambiguationData":[OSD([subQ0])]});var subQ3=sQuery(id+"F10.wireOp",EDGE,"E42.top");var subQ4=sQuery(id+"F6.wireOp",EDGE,"E31.left");var subQ8=sQuery(id+"F0.wireOp",EDGE,"E0.bottom");var subQ11=sQuery(id+"F0.wireOp",EDGE,"E0.right");var subQ13=sQuery(id+"F0.wireOp",EDGE,"E0.left");var subQ15=sQuery(id+"F0.wireOp",EDGE,"E0.top");var subQ19=sQuery(id+"F0.wireOp",EDGE,"E9");var subQ24=sQuery(id+"F0.wireOp",EDGE,"E8");var subQ26=sQuery(id+"F0.wireOp",EDGE,"E2");var subQ28=sQuery(id+"F0.wireOp",EDGE,"E10");var subQ30=sQuery(id+"F0.wireOp",EDGE,"E11");Q0=makeQuery(id+"F22.boolean.opBoolean","SPLIT",FACE,{"disambiguationData":[TD([subQ1])],"derivedFrom":makeQuery(id+"F20.boolean.opBoolean","SPLIT",FACE,{"disambiguationData":[TD([subQ1])],"derivedFrom":makeQuery(id+"F15.boolean.opBoolean","MERGE",FACE,{"derivedFrom":[makeQuery(id+"F11.boolean.opBoolean","MERGE",FACE,{"derivedFrom":[makeQuery(id+"F7.boolean.opBoolean","MERGE",FACE,{"derivedFrom":[makeQuery(id+"F1.opExtrude","CAP_FACE",FACE,{"disambiguationData":[OSD([subQ8,subQ15,subQ13,subQ11,subQ26,subQ24,subQ19,subQ28,subQ30])],"isStart":true}),makeQuery(id+"F7.opExtrude","SWEPT_FACE",FACE,{"disambiguationData":[OSD([subQ4])]})]}),makeQuery(id+"F11.opExtrude","SWEPT_FACE",FACE,{"disambiguationData":[OSD([subQ3])]})]}),makeQuery(id+"F15.opExtrude","SWEPT_FACE",FACE,{"disambiguationData":[OSD([subQ0])]})]})})});}
            var sketch = newSketch(context, id + "F25", { "sketchPlane" : qUnion([Q0])});
            skLineSegment(sketch, "E77.bottom", {"start": v(-16, 19) * mm, "end": v(-6, 19) * mm});
            skLineSegment(sketch, "E77.top", {"start": v(-16, -41) * mm, "end": v(-6, -41) * mm});
            skLineSegment(sketch, "E77.left", {"start": v(-16, 19) * mm, "end": v(-16, -41) * mm});
            skLineSegment(sketch, "E77.right", {"start": v(-6, 19) * mm, "end": v(-6, -41) * mm});
            skLineSegment(sketch, "E78.bottom", {"start": v(-6, 16) * mm, "end": v(2, 16) * mm});
            skLineSegment(sketch, "E78.top", {"start": v(-6, 0) * mm, "end": v(2, 0) * mm});
            skLineSegment(sketch, "E78.left", {"start": v(-6, 16) * mm, "end": v(-6, 0) * mm});
            skLineSegment(sketch, "E78.right", {"start": v(2, 16) * mm, "end": v(2, 0) * mm});
            skSolve(sketch);
        }
        {
            var Q0;
            Q0 = qSketchRegion(id + "F25", true);
            extrude(context, id + "F26", {"entities" : qUnion([Q0]), "oppositeDirection" : true, "depth" : 5 * mm});
        }
    });
